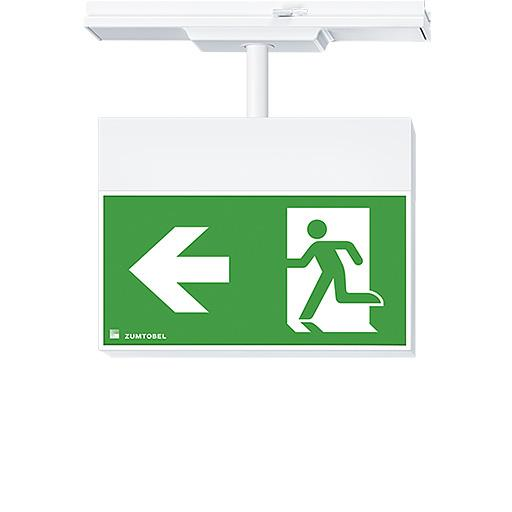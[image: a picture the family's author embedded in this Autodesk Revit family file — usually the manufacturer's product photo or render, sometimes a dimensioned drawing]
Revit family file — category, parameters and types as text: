
# Revit family: Zumtobel TECTON 2 continuous row element CROSSIGN 110 P
name_source: partatom
category: Lighting Fixtures
units: mm (PartAtom-declared; Revit-internal decimal feet)

## family parameters
Cut with Voids When Loaded = No
Host = Face
Light Source = No
Maintain Annotation Orientation = No
Part Type = Normal
Room Calculation Point = Yes
Round Connector Dimension = Use Diameter
Shared = No

## types (9) — shared parameters
Apparent Load = 7 VA
Assembly Code = Pr_75_75_63_27
Description = Emergency exit signs
Export Type to IFC As = IfcLightFixtureType
Housing Black = No
Housing White = Yes
Lamp = LED
Luminaire Height = 175.6 mm  [stored 0.576115 ft]
Luminaire Length = 250 mm  [stored 0.82021 ft]
Luminaire Width = 60 mm  [stored 0.19685 ft]
Manufacturer = Zumtobel Lighting
Power Factor = 0.8
Type Adapter = Zumtobel-Parts-TECTON 2-Adapter-CROSSIGN : White
Type Adapter BK = Zumtobel-Parts-TECTON 2-Adapter-CROSSIGN : Black
Type Adapter WH = Zumtobel-Parts-TECTON 2-Adapter-CROSSIGN : White
Type Housing = Zumtobel-Parts-TECTON-CROSSIGN 110 P-Safety sign-Assembled : White
Type Housing Black = Zumtobel-Parts-TECTON-CROSSIGN 110 P-Safety sign-Assembled : Black
Type Housing White = Zumtobel-Parts-TECTON-CROSSIGN 110 P-Safety sign-Assembled : White
Type IFC Predefined Type = SECURITYLIGHTING
URL = https://www.zumtobel.com
zero-valued in all types: Default Elevation

## per-type parameters (varying)
| type | ERI Escape Route Illumination | Model | Type Image | Type Light Source |
| CROSSIGN 110 P TEC2 E1D ERI WH | Yes | 70515682 | ZS_ONL_F_CRO_110_TECTON-II_RZ-L_ERI_GP_WH.jpg | Zumtobel-Light Sources-TECTON 2-CROSSIGN-110 P : 70515682_(STD_LEO).IES |
| CROSSIGN 110 P TEC2 E1D WH | No | 70515681 | ZS_ONL_F_CRO_110_TECTON-II_RZ-L_GP_WH.jpg | Zumtobel-Light Sources-TECTON 2-CROSSIGN-110 P : 70515681_(STD_LEO).IES |
| CROSSIGN 110 P TEC2 E3D ERI WH | Yes | 70515684 | ZS_ONL_F_CRO_110_TECTON-II_RZ-L_ERI_GP_WH.jpg | Zumtobel-Light Sources-TECTON 2-CROSSIGN-110 P : 70515684_(STD_LEO).IES |
| CROSSIGN 110 P TEC2 E3D WH | No | 70515683 | ZS_ONL_F_CRO_110_TECTON-II_RZ-L_GP_WH.jpg | Zumtobel-Light Sources-TECTON 2-CROSSIGN-110 P : 70515683_(STD_LEO).IES |
| CROSSIGN 110 P TEC2 ECC WH | No | 70515688 | ZS_ONL_F_CRO_110_TECTON-II_RZ-L_GP_WH.jpg | Zumtobel-Light Sources-TECTON 2-CROSSIGN-110 P : 70515688_(STD_LEO).IES |
| CROSSIGN 110 P TEC2 ECD ERI WH | Yes | 70515687 | ZS_ONL_F_CRO_110_TECTON-II_RZ-L_ERI_GP_WH.jpg | Zumtobel-Light Sources-TECTON 2-CROSSIGN-110 P : 70515687_(STD_LEO).IES |
| CROSSIGN 110 P TEC2 ECP ERI WH | Yes | 70515686 | ZS_ONL_F_CRO_110_TECTON-II_RZ-L_ERI_GP_WH.jpg | Zumtobel-Light Sources-TECTON 2-CROSSIGN-110 P : 70515686_(STD_LEO).IES |
| CROSSIGN 110 P TEC2 ECP WH | No | 70515685 | ZS_ONL_F_CRO_110_TECTON-II_RZ-L_GP_WH.jpg | Zumtobel-Light Sources-TECTON 2-CROSSIGN-110 P : 70515685_(STD_LEO).IES |
| CROSSIGN 110 P TEC2 ELP WH | No | 70515689 | ZS_ONL_F_CRO_110_TECTON-II_RZ-L_GP_WH.jpg | Zumtobel-Light Sources-TECTON 2-CROSSIGN-110 P : 70515689_(STD_LEO).IES |

note: [stored X ft] marks values corroborated as IEEE doubles in the binary element streams (Revit-internal decimal feet)

## geometry (parser evidence)
native form markers: Sweep x15
no freeform markers — native parametric forms only
